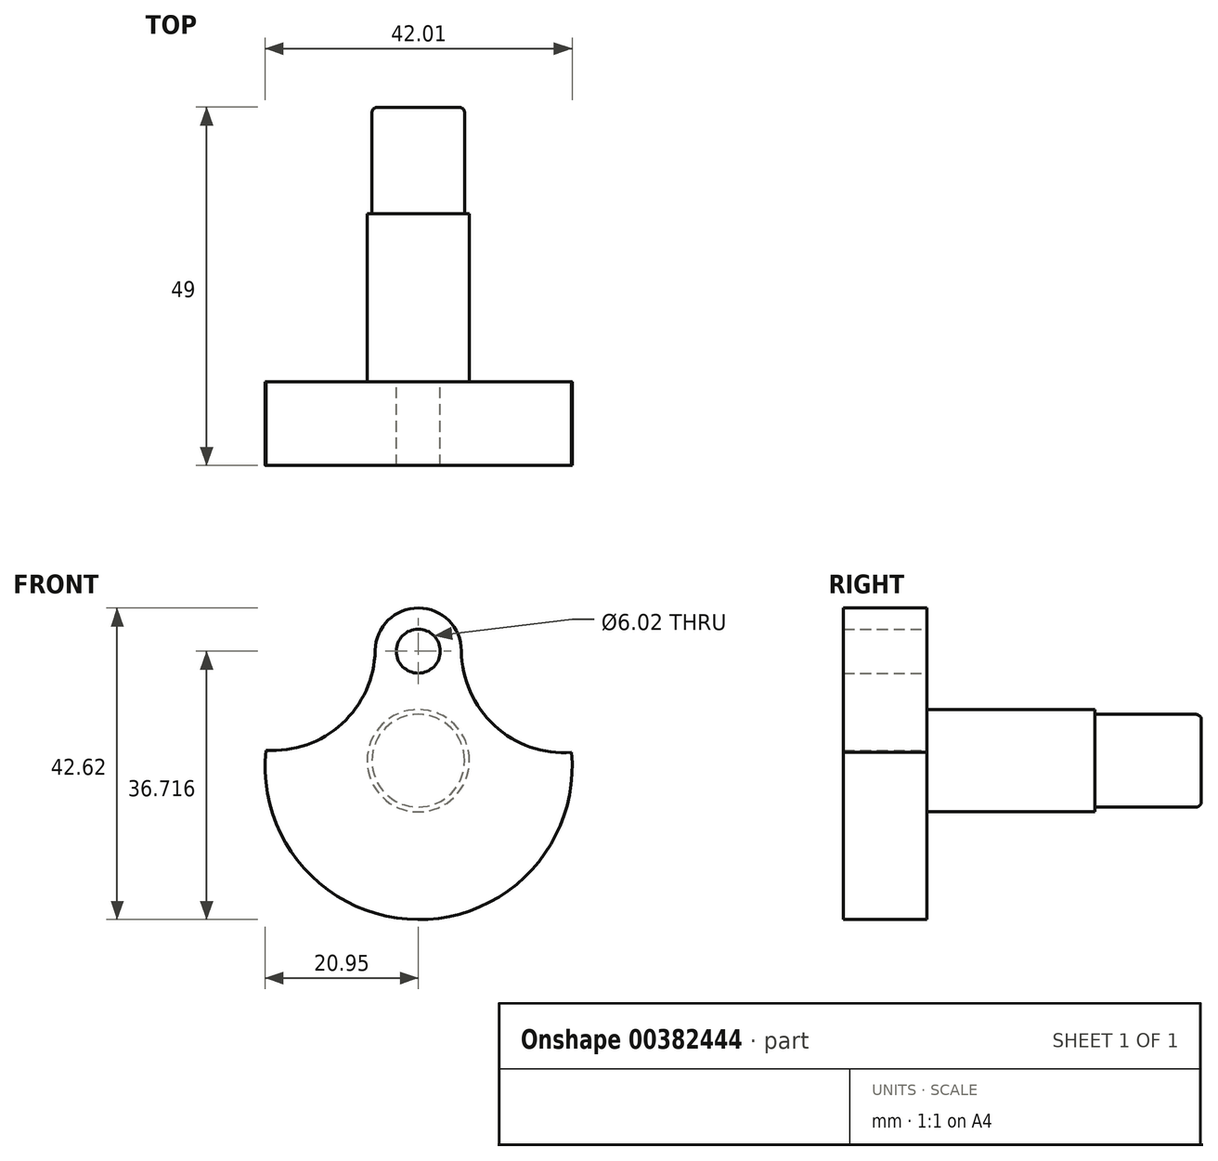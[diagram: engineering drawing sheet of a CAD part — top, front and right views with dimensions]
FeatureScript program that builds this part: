
annotation { "Feature Type Name" : "Feature", "Feature Type Description" : "" }
export const myFeature = defineFeature(function(context is Context, id is Id, definition is map)
    precondition{}
    {
        {
            var Q0;
            Q0=qCreatedBy(makeId("Front.planeOp"),FACE);
            var sketch = newSketch(context, id + "F0", { "sketchPlane" : qUnion([Q0])});
            skCircle(sketch, "E0", {"center": v(0, 14.99) * mm, "radius": 3 * mm});
            skArc(sketch, "E1", {"start": v(5.9, 15.02) * mm, "mid": v(0.04, 20.9) * mm, "end": v(-5.9, 15.1) * mm});
            skArc(sketch, "E2", {"start": v(5.9, 15.02) * mm, "mid": v(10.42, 4.8) * mm, "end": v(20.98, 1.15) * mm});
            skArc(sketch, "E3", {"start": v(-20.84, 1.42) * mm, "mid": v(-10.44, 5.06) * mm, "end": v(-5.9, 15.1) * mm});
            skArc(sketch, "E4.trimOffspring", {"start": v(-20.84, 1.42) * mm, "mid": v(-0.08, -21.73) * mm, "end": v(20.98, 1.15) * mm});
            skSolve(sketch);
        }
        {
            var Q0;
            Q0 = qSketchRegion(id + "F0", true);
            extrude(context, id + "F1", {"entities" : qUnion([Q0]), "depth" : 11.43 * mm});
        }
        {
            var Q0;
            Q0=qCreatedBy(makeId("Front.planeOp"),FACE);
            var sketch = newSketch(context, id + "F2", { "sketchPlane" : qUnion([Q0])});
            skCircle(sketch, "E5", {"center": v(0, 0) * mm, "radius": 7 * mm});
            skCircle(sketch, "E6", {"center": v(0, 0) * mm, "radius": 6.34 * mm});
            skSolve(sketch);
        }
        {
            var Q0;
            Q0=makeQuery(id+"F2.imprint","IMPRINT",FACE,{"disambiguationData":[TD([[makeQuery(id+"F2.imprint","IMPRINT",EDGE,{"derivedFrom":sQuery(id+"F2.wireOp",EDGE,"E5")}),1.0]])]});
            extrude(context, id + "F3", {"entities" : qUnion([Q0]), "operationType" : NewBodyOperationType.ADD, "oppositeDirection" : true, "depth" : 23.01 * mm});
        }
        {
            var Q0;
            Q0=makeQuery(id+"F2.imprint","IMPRINT",FACE,{"disambiguationData":[TD([[makeQuery(id+"F2.imprint","IMPRINT",EDGE,{"derivedFrom":sQuery(id+"F2.wireOp",EDGE,"E6")}),1.0]])]});
            extrude(context, id + "F4", {"entities" : qUnion([Q0]), "operationType" : NewBodyOperationType.ADD, "oppositeDirection" : true, "depth" : 37.57 * mm});
        }
        {
            var Q0;
            Q0=makeQuery(id+"F4.opExtrude","CAP_EDGE",EDGE,{"disambiguationData":[OSD([sQuery(id+"F2.wireOp",EDGE,"E6")])],"isStart":false});
            fillet(context, id + "F5", {"entities" : qUnion([Q0]), "radius" : 0.76 * mm, "tangentPropagation" : true, "allowEdgeOverflow" : false});
        }
    });
